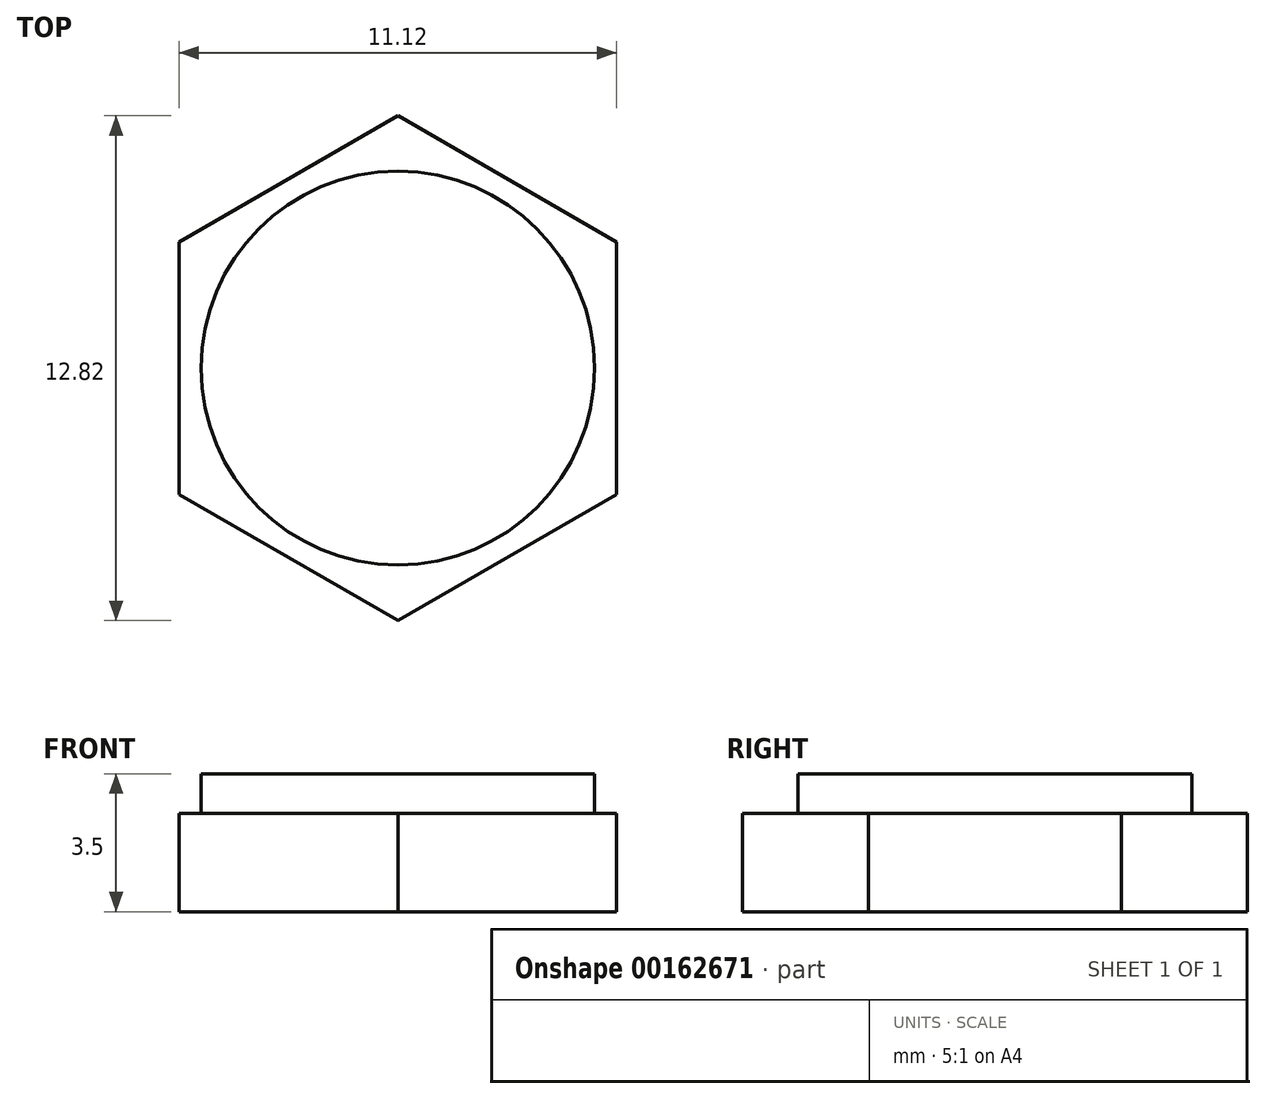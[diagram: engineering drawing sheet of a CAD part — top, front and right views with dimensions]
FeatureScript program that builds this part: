
annotation { "Feature Type Name" : "Feature", "Feature Type Description" : "" }
export const myFeature = defineFeature(function(context is Context, id is Id, definition is map)
    precondition{}
    {
        {
            var Q0;
            Q0=qCreatedBy(makeId("Top.planeOp"),FACE);
            var sketch = newSketch(context, id + "F0", { "sketchPlane" : qUnion([Q0])});
            skCircle(sketch, "E0.cCircle", {"center": v(0, 0) * mm, "radius": 5.55 * mm, "construction": true});
            skLineSegment(sketch, "E0.0", {"start": v(-5.55, -3.2) * mm, "end": v(-5.55, 3.2) * mm});
            skLineSegment(sketch, "E0.1", {"start": v(-5.55, 3.2) * mm, "end": v(0, 6.41) * mm});
            skLineSegment(sketch, "E0.2", {"start": v(0, 6.41) * mm, "end": v(5.55, 3.2) * mm});
            skLineSegment(sketch, "E0.3", {"start": v(5.55, 3.2) * mm, "end": v(5.56, -3.2) * mm});
            skLineSegment(sketch, "E0.4", {"start": v(5.56, -3.2) * mm, "end": v(0, -6.41) * mm});
            skLineSegment(sketch, "E0.5", {"start": v(0, -6.41) * mm, "end": v(-5.55, -3.2) * mm});
            skPoint(sketch, "E0.0.midPoint", {"position": v(-5.55, 0) * mm});
            skCircle(sketch, "E1", {"center": v(0, 0) * mm, "radius": 5 * mm});
            skSolve(sketch);
        }
        {
            var Q0;
            Q0 = qSketchRegion(id + "F0", true);
            var Q1;
            Q1=makeQuery(id+"F0.imprint","IMPRINT",FACE,{"disambiguationData":[TD([[makeQuery(id+"F0.imprint","IMPRINT",EDGE,{"derivedFrom":sQuery(id+"F0.wireOp",EDGE,"E1")}),1.0]])]});
            extrude(context, id + "F1", {"entities" : qUnion([Q0, Q1]), "depth" : 2.5 * mm, "offsetDistance" : 25 * mm});
        }
        {
            var Q0;
            Q0=makeQuery(id+"F0.imprint","IMPRINT",FACE,{"disambiguationData":[TD([[makeQuery(id+"F0.imprint","IMPRINT",EDGE,{"derivedFrom":sQuery(id+"F0.wireOp",EDGE,"E1")}),1.0]])]});
            extrude(context, id + "F2", {"entities" : qUnion([Q0]), "operationType" : NewBodyOperationType.ADD, "depth" : 3.5 * mm, "offsetDistance" : 25 * mm});
        }
    });
